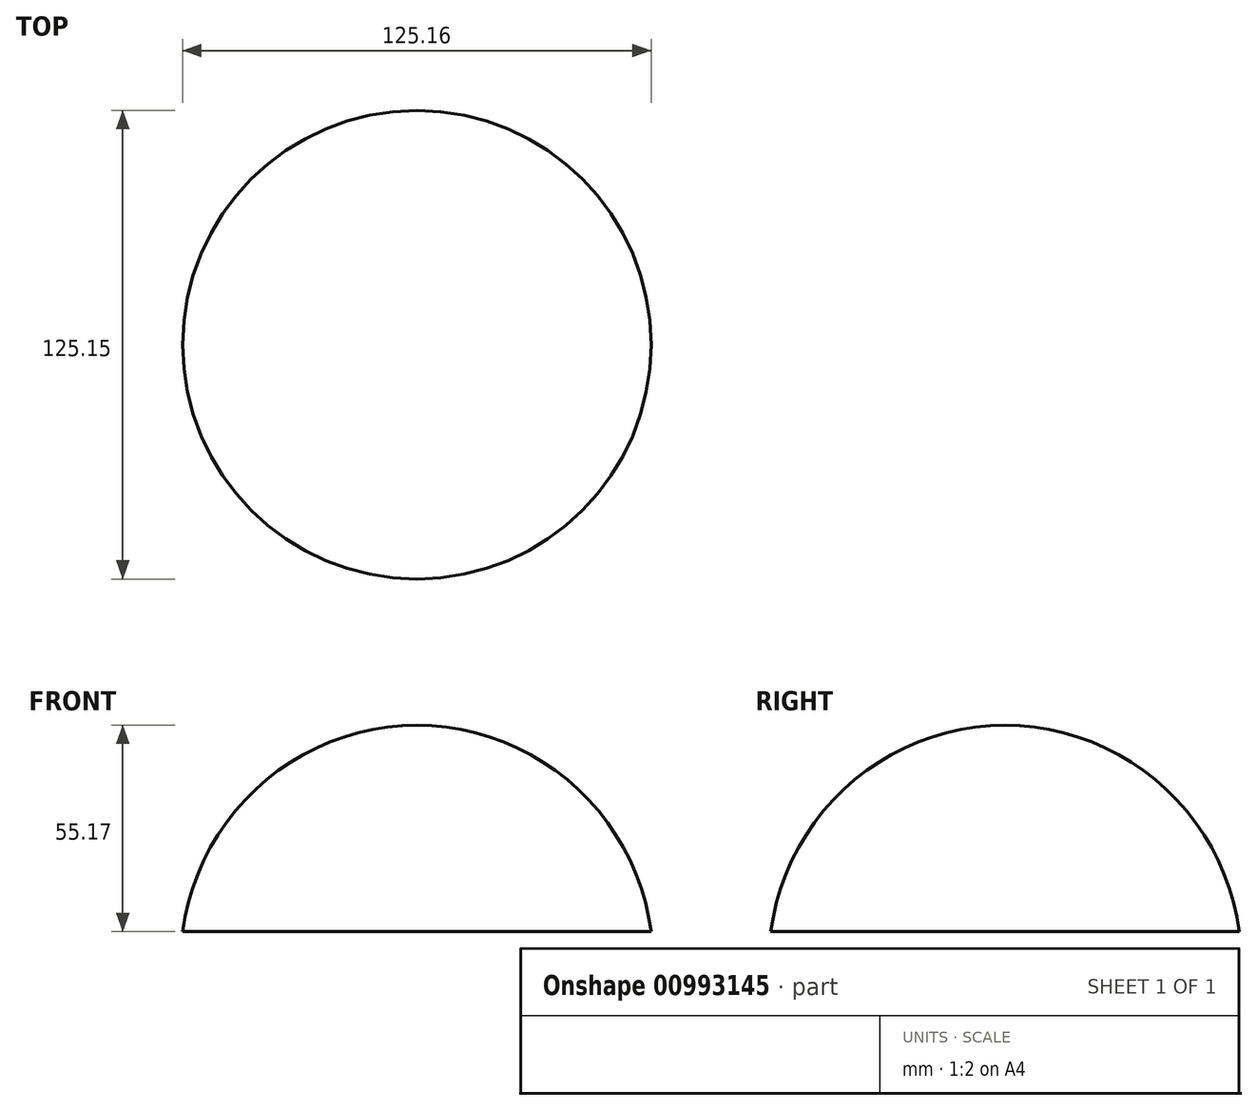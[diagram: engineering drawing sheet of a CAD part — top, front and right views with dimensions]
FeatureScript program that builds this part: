
annotation { "Feature Type Name" : "Feature", "Feature Type Description" : "" }
export const myFeature = defineFeature(function(context is Context, id is Id, definition is map)
    precondition{}
    {
        {
            var Q0;
            Q0=qCreatedBy(makeId("Right.planeOp"),FACE);
            var sketch = newSketch(context, id + "F0", { "sketchPlane" : qUnion([Q0])});
            skLineSegment(sketch, "E0", {"start": v(-29.19, 55.17) * mm, "end": v(-29.19, -71.83) * mm});
            skArc(sketch, "E1", {"start": v(-29.19, 55.17) * mm, "mid": v(-92.31, -8.33) * mm, "end": v(-29.19, -71.83) * mm});
            skSolve(sketch);
        }
        {
            var Q0;
            Q0=makeQuery(id+"F0.imprint","IMPRINT",FACE,{"disambiguationData":[TD([[makeQuery(id+"F0.imprint","IMPRINT",EDGE,{"derivedFrom":sQuery(id+"F0.wireOp",EDGE,"E0")}),-1.0]])]});
            var Q1;
            Q1=sQuery(id+"F0.wireOp",EDGE,"E0");
            revolve(context, id + "F1", {"surfaceOperationType" : NewSurfaceOperationType.NEW, "entities" : qUnion([Q0]), "axis" : qUnion([Q1]), "revolveType" : RevolveType.FULL});
        }
        {
            var Q0;
            Q0=qCreatedBy(makeId("Front.planeOp"),FACE);
            var sketch = newSketch(context, id + "F2", { "sketchPlane" : qUnion([Q0])});
            skLineSegment(sketch, "E2.bottom", {"start": v(76.3, 0) * mm, "end": v(-76.94, 0) * mm});
            skLineSegment(sketch, "E2.top", {"start": v(76.3, -83.89) * mm, "end": v(-76.94, -83.89) * mm});
            skLineSegment(sketch, "E2.left", {"start": v(76.3, 0) * mm, "end": v(76.3, -83.89) * mm});
            skLineSegment(sketch, "E2.right", {"start": v(-76.94, 0) * mm, "end": v(-76.94, -83.89) * mm});
            skSolve(sketch);
        }
        {
            var Q0;
            Q0=makeQuery(id+"F2.imprint","IMPRINT",FACE,{"disambiguationData":[TD([[makeQuery(id+"F2.imprint","IMPRINT",EDGE,{"derivedFrom":sQuery(id+"F2.wireOp",EDGE,"E2.bottom")}),1.0]])]});
            extrude(context, id + "F3", {"entities" : qUnion([Q0]), "operationType" : NewBodyOperationType.REMOVE, "oppositeDirection" : true, "depth" : 50.8 * mm, "offsetDistance" : 25.4 * mm, "hasSecondDirection" : true, "secondDirectionOppositeDirection" : false, "secondDirectionDepth" : 127 * mm});
        }
    });
